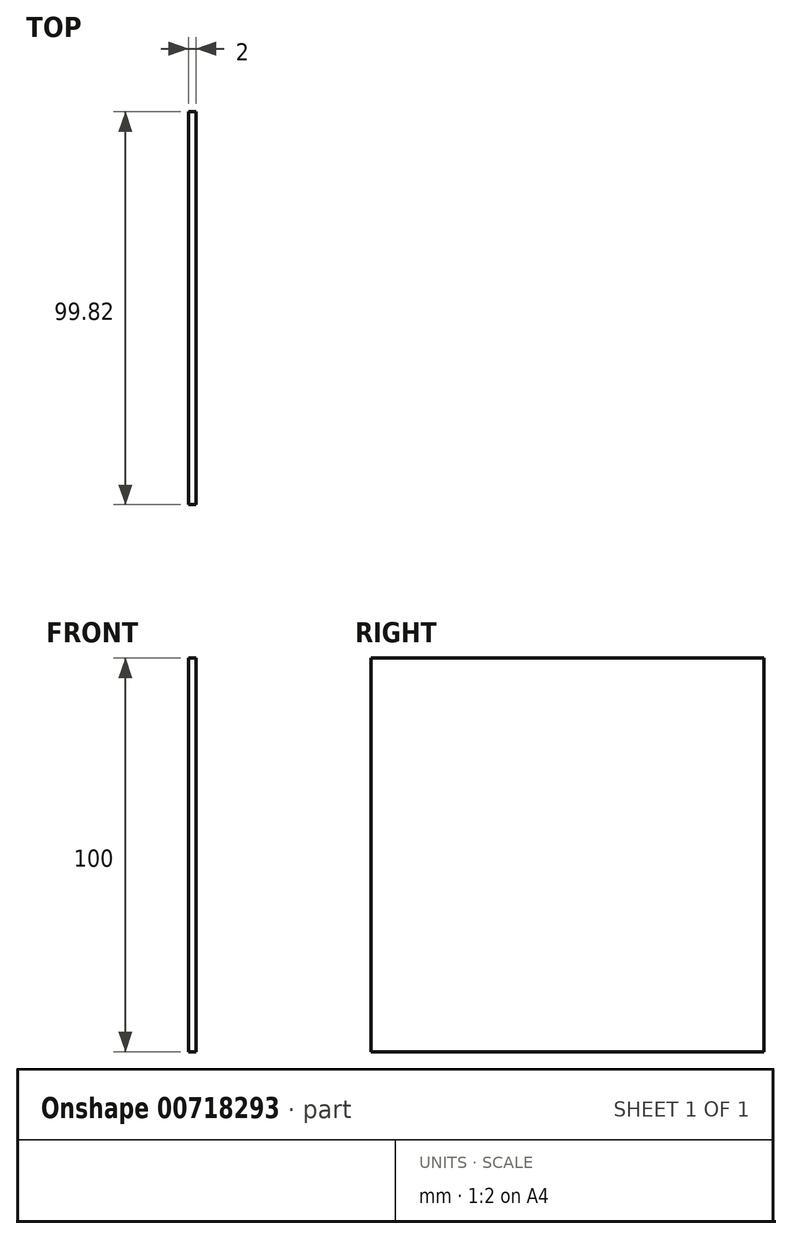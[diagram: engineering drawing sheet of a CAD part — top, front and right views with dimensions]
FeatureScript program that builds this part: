
annotation { "Feature Type Name" : "Feature", "Feature Type Description" : "" }
export const myFeature = defineFeature(function(context is Context, id is Id, definition is map)
    precondition{}
    {
        {
            var Q0;
            Q0=qCreatedBy(makeId("Top.planeOp"),FACE);
            var sketch = newSketch(context, id + "F0", { "sketchPlane" : qUnion([Q0])});
            skCircle(sketch, "E0", {"center": v(0, 0) * mm, "radius": 50 * mm});
            skSolve(sketch);
        }
        {
            var Q0;
            Q0=makeQuery(id+"F0.imprint","IMPRINT",FACE,{"disambiguationData":[TD([[makeQuery(id+"F0.imprint","IMPRINT",EDGE,{"derivedFrom":sQuery(id+"F0.wireOp",EDGE,"E0")}),1.0]])]});
            var sketch = newSketch(context, id + "F1", { "sketchPlane" : qUnion([Q0])});
            skPoint(sketch, "E1", {"position": v(2, 0) * mm});
            skPoint(sketch, "E2.0.1.0", {"position": v(4, 0) * mm});
            skPoint(sketch, "E2.0.2.0", {"position": v(6, 0) * mm});
            skPoint(sketch, "E2.0.3.0", {"position": v(8, 0) * mm});
            skPoint(sketch, "E2.0.4.0", {"position": v(10, 0) * mm});
            skPoint(sketch, "E2.0.5.0", {"position": v(12, 0) * mm});
            skPoint(sketch, "E2.0.6.0", {"position": v(14, 0) * mm});
            skPoint(sketch, "E2.0.7.0", {"position": v(16, 0) * mm});
            skPoint(sketch, "E2.0.8.0", {"position": v(18, 0) * mm});
            skPoint(sketch, "E2.0.9.0", {"position": v(20, 0) * mm});
            skPoint(sketch, "E2.0.10.0", {"position": v(22, 0) * mm});
            skPoint(sketch, "E2.0.11.0", {"position": v(24, 0) * mm});
            skPoint(sketch, "E2.0.12.0", {"position": v(26, 0) * mm});
            skPoint(sketch, "E2.0.13.0", {"position": v(28, 0) * mm});
            skPoint(sketch, "E2.0.14.0", {"position": v(30, 0) * mm});
            skPoint(sketch, "E2.0.15.0", {"position": v(32, 0) * mm});
            skPoint(sketch, "E2.0.16.0", {"position": v(34, 0) * mm});
            skPoint(sketch, "E2.0.17.0", {"position": v(36, 0) * mm});
            skPoint(sketch, "E2.0.18.0", {"position": v(38, 0) * mm});
            skPoint(sketch, "E2.0.19.0", {"position": v(40, 0) * mm});
            skPoint(sketch, "E2.0.20.0", {"position": v(42, 0) * mm});
            skPoint(sketch, "E2.0.21.0", {"position": v(44, 0) * mm});
            skPoint(sketch, "E2.0.22.0", {"position": v(46, 0) * mm});
            skPoint(sketch, "E2.0.23.0", {"position": v(48, 0) * mm});
            skPoint(sketch, "E2.0.24.0", {"position": v(50, 0) * mm});
            skPoint(sketch, "E3", {"position": v(-2, 0) * mm});
            skPoint(sketch, "E4.1.0.0", {"position": v(-4, 0) * mm});
            skPoint(sketch, "E4.2.0.0", {"position": v(-6, 0) * mm});
            skPoint(sketch, "E4.3.0.0", {"position": v(-8, 0) * mm});
            skPoint(sketch, "E4.4.0.0", {"position": v(-10, 0) * mm});
            skPoint(sketch, "E4.5.0.0", {"position": v(-12, 0) * mm});
            skPoint(sketch, "E4.6.0.0", {"position": v(-14, 0) * mm});
            skPoint(sketch, "E4.7.0.0", {"position": v(-16, 0) * mm});
            skPoint(sketch, "E4.8.0.0", {"position": v(-18, 0) * mm});
            skPoint(sketch, "E4.9.0.0", {"position": v(-20, 0) * mm});
            skPoint(sketch, "E4.10.0.0", {"position": v(-22, 0) * mm});
            skPoint(sketch, "E4.11.0.0", {"position": v(-24, 0) * mm});
            skPoint(sketch, "E4.12.0.0", {"position": v(-26, 0) * mm});
            skPoint(sketch, "E4.13.0.0", {"position": v(-28, 0) * mm});
            skPoint(sketch, "E4.14.0.0", {"position": v(-30, 0) * mm});
            skPoint(sketch, "E4.15.0.0", {"position": v(-32, 0) * mm});
            skPoint(sketch, "E4.16.0.0", {"position": v(-34, 0) * mm});
            skPoint(sketch, "E4.17.0.0", {"position": v(-36, 0) * mm});
            skPoint(sketch, "E4.18.0.0", {"position": v(-38, 0) * mm});
            skPoint(sketch, "E4.19.0.0", {"position": v(-40, 0) * mm});
            skPoint(sketch, "E4.20.0.0", {"position": v(-42, 0) * mm});
            skPoint(sketch, "E4.21.0.0", {"position": v(-44, 0) * mm});
            skPoint(sketch, "E4.22.0.0", {"position": v(-46, 0) * mm});
            skPoint(sketch, "E4.23.0.0", {"position": v(-48, 0) * mm});
            skPoint(sketch, "E4.24.0.0", {"position": v(-50, 0) * mm});
            skLineSegment(sketch, "E4.direction1", {"start": v(-2, 0) * mm, "end": v(-4, 0) * mm, "construction": true});
            skLineSegment(sketch, "E5", {"start": v(0, 0) * mm, "end": v(2, 0) * mm});
            skLineSegment(sketch, "E6", {"start": v(8, 0) * mm, "end": v(10, 0) * mm});
            skLineSegment(sketch, "E7", {"start": v(12, 0) * mm, "end": v(14, 0) * mm});
            skLineSegment(sketch, "E8", {"start": v(16, 0) * mm, "end": v(18, 0) * mm});
            skLineSegment(sketch, "E9", {"start": v(14, 0) * mm, "end": v(16, 0) * mm});
            skLineSegment(sketch, "E10", {"start": v(10, 0) * mm, "end": v(12, 0) * mm});
            skLineSegment(sketch, "E11", {"start": v(6, 0) * mm, "end": v(8, 0) * mm});
            skLineSegment(sketch, "E12", {"start": v(2, 0) * mm, "end": v(4, 0) * mm});
            skLineSegment(sketch, "E13", {"start": v(4, 0) * mm, "end": v(6, 0) * mm});
            skLineSegment(sketch, "E14", {"start": v(18, 0) * mm, "end": v(20, 0) * mm});
            skLineSegment(sketch, "E15", {"start": v(20, 0) * mm, "end": v(22, 0) * mm});
            skLineSegment(sketch, "E16", {"start": v(22, 0) * mm, "end": v(24, 0) * mm});
            skLineSegment(sketch, "E17", {"start": v(24, 0) * mm, "end": v(26, 0) * mm});
            skLineSegment(sketch, "E18", {"start": v(26, 0) * mm, "end": v(28, 0) * mm});
            skLineSegment(sketch, "E19", {"start": v(28, 0) * mm, "end": v(30, 0) * mm});
            skLineSegment(sketch, "E20", {"start": v(30, 0) * mm, "end": v(32, 0) * mm});
            skLineSegment(sketch, "E21", {"start": v(32, 0) * mm, "end": v(34, 0) * mm});
            skLineSegment(sketch, "E22", {"start": v(34, 0) * mm, "end": v(36, 0) * mm});
            skLineSegment(sketch, "E23", {"start": v(36, 0) * mm, "end": v(38, 0) * mm});
            skLineSegment(sketch, "E24", {"start": v(38, 0) * mm, "end": v(40, 0) * mm});
            skLineSegment(sketch, "E25", {"start": v(40, 0) * mm, "end": v(42, 0) * mm});
            skLineSegment(sketch, "E26", {"start": v(42, 0) * mm, "end": v(44, 0) * mm});
            skLineSegment(sketch, "E27", {"start": v(44, 0) * mm, "end": v(46, 0) * mm});
            skLineSegment(sketch, "E28", {"start": v(46, 0) * mm, "end": v(48, 0) * mm});
            skLineSegment(sketch, "E29", {"start": v(0, 0) * mm, "end": v(-2, 0) * mm});
            skLineSegment(sketch, "E30.1.0.0", {"start": v(-2, 0) * mm, "end": v(-4, 0) * mm});
            skLineSegment(sketch, "E30.2.0.0", {"start": v(-4, 0) * mm, "end": v(-6, 0) * mm});
            skLineSegment(sketch, "E30.3.0.0", {"start": v(-6, 0) * mm, "end": v(-8, 0) * mm});
            skLineSegment(sketch, "E30.4.0.0", {"start": v(-8, 0) * mm, "end": v(-10, 0) * mm});
            skLineSegment(sketch, "E30.5.0.0", {"start": v(-10, 0) * mm, "end": v(-12, 0) * mm});
            skLineSegment(sketch, "E30.6.0.0", {"start": v(-12, 0) * mm, "end": v(-14, 0) * mm});
            skLineSegment(sketch, "E30.7.0.0", {"start": v(-14, 0) * mm, "end": v(-16, 0) * mm});
            skLineSegment(sketch, "E30.8.0.0", {"start": v(-16, 0) * mm, "end": v(-18, 0) * mm});
            skLineSegment(sketch, "E30.9.0.0", {"start": v(-18, 0) * mm, "end": v(-20, 0) * mm});
            skLineSegment(sketch, "E30.10.0.0", {"start": v(-20, 0) * mm, "end": v(-22, 0) * mm});
            skLineSegment(sketch, "E30.11.0.0", {"start": v(-22, 0) * mm, "end": v(-24, 0) * mm});
            skLineSegment(sketch, "E30.12.0.0", {"start": v(-24, 0) * mm, "end": v(-26, 0) * mm});
            skLineSegment(sketch, "E30.13.0.0", {"start": v(-26, 0) * mm, "end": v(-28, 0) * mm});
            skLineSegment(sketch, "E30.14.0.0", {"start": v(-28, 0) * mm, "end": v(-30, 0) * mm});
            skLineSegment(sketch, "E30.15.0.0", {"start": v(-30, 0) * mm, "end": v(-32, 0) * mm});
            skLineSegment(sketch, "E30.16.0.0", {"start": v(-32, 0) * mm, "end": v(-34, 0) * mm});
            skLineSegment(sketch, "E30.17.0.0", {"start": v(-34, 0) * mm, "end": v(-36, 0) * mm});
            skLineSegment(sketch, "E30.18.0.0", {"start": v(-36, 0) * mm, "end": v(-38, 0) * mm});
            skLineSegment(sketch, "E30.19.0.0", {"start": v(-38, 0) * mm, "end": v(-40, 0) * mm});
            skLineSegment(sketch, "E30.20.0.0", {"start": v(-40, 0) * mm, "end": v(-42, 0) * mm});
            skLineSegment(sketch, "E30.21.0.0", {"start": v(-42, 0) * mm, "end": v(-44, 0) * mm});
            skLineSegment(sketch, "E30.22.0.0", {"start": v(-44, 0) * mm, "end": v(-46, 0) * mm});
            skLineSegment(sketch, "E30.23.0.0", {"start": v(-46, 0) * mm, "end": v(-48, 0) * mm});
            skLineSegment(sketch, "E30.24.0.0", {"start": v(-48, 0) * mm, "end": v(-50, 0) * mm});
            skLineSegment(sketch, "E31", {"start": v(0, 0) * mm, "end": v(0, 50) * mm});
            skLineSegment(sketch, "E32", {"start": v(2, 0) * mm, "end": v(2, 49.91) * mm});
            skLineSegment(sketch, "E33", {"start": v(4, 0) * mm, "end": v(4, 49.83) * mm});
            skLineSegment(sketch, "E34", {"start": v(6, 0) * mm, "end": v(6, 49.6) * mm});
            skLineSegment(sketch, "E35", {"start": v(8, 0) * mm, "end": v(8, 49.33) * mm});
            skLineSegment(sketch, "E36", {"start": v(10, 0) * mm, "end": v(10, 48.95) * mm});
            skLineSegment(sketch, "E37", {"start": v(12, 0) * mm, "end": v(12, 48.5) * mm});
            skLineSegment(sketch, "E38", {"start": v(14, 0) * mm, "end": v(14, 47.96) * mm});
            skLineSegment(sketch, "E39", {"start": v(16, 0) * mm, "end": v(16, 47.33) * mm});
            skLineSegment(sketch, "E40", {"start": v(18, 0) * mm, "end": v(18, 46.61) * mm});
            skLineSegment(sketch, "E41", {"start": v(20, 0) * mm, "end": v(20, 45.78) * mm});
            skLineSegment(sketch, "E42", {"start": v(22, 0) * mm, "end": v(22, 44.86) * mm});
            skLineSegment(sketch, "E43", {"start": v(24, 0) * mm, "end": v(24, 43.82) * mm});
            skLineSegment(sketch, "E44", {"start": v(26, 0) * mm, "end": v(26, 42.66) * mm});
            skLineSegment(sketch, "E45", {"start": v(28, 0) * mm, "end": v(28, 41.4) * mm});
            skLineSegment(sketch, "E46", {"start": v(30, 0) * mm, "end": v(30, 39.94) * mm});
            skLineSegment(sketch, "E47", {"start": v(32, 0) * mm, "end": v(32, 38.4) * mm});
            skLineSegment(sketch, "E48", {"start": v(34, 0) * mm, "end": v(34, 36.6) * mm});
            skLineSegment(sketch, "E49", {"start": v(36, 0) * mm, "end": v(36, 34.65) * mm});
            skLineSegment(sketch, "E50", {"start": v(38, 0) * mm, "end": v(38, 32.47) * mm});
            skLineSegment(sketch, "E51", {"start": v(40, 0) * mm, "end": v(40, 29.93) * mm});
            skLineSegment(sketch, "E52", {"start": v(42, 0) * mm, "end": v(42, 27.04) * mm});
            skLineSegment(sketch, "E53", {"start": v(44, 0) * mm, "end": v(44, 23.66) * mm});
            skLineSegment(sketch, "E54", {"start": v(46, 0) * mm, "end": v(46, 19.48) * mm});
            skLineSegment(sketch, "E55", {"start": v(48, 0) * mm, "end": v(48, 13.88) * mm});
            skLineSegment(sketch, "E56", {"start": v(48, 0) * mm, "end": v(49.75, 0) * mm});
            skLineSegment(sketch, "E57", {"start": v(49.75, 0) * mm, "end": v(49.75, 4.8) * mm});
            skLineSegment(sketch, "E58", {"start": v(49.75, 4.8) * mm, "end": v(48, 4.8) * mm});
            skLineSegment(sketch, "E59", {"start": v(48, 13.88) * mm, "end": v(46, 13.88) * mm});
            skLineSegment(sketch, "E60", {"start": v(46, 19.48) * mm, "end": v(44, 19.48) * mm});
            skLineSegment(sketch, "E61", {"start": v(44, 23.66) * mm, "end": v(42, 23.66) * mm});
            skLineSegment(sketch, "E62", {"start": v(42, 27.04) * mm, "end": v(40, 27.04) * mm});
            skLineSegment(sketch, "E63", {"start": v(40, 29.93) * mm, "end": v(38, 29.93) * mm});
            skLineSegment(sketch, "E64", {"start": v(38, 32.47) * mm, "end": v(36, 32.47) * mm});
            skLineSegment(sketch, "E65", {"start": v(36, 34.65) * mm, "end": v(34, 34.65) * mm});
            skLineSegment(sketch, "E66", {"start": v(34, 36.6) * mm, "end": v(32, 36.6) * mm});
            skLineSegment(sketch, "E67", {"start": v(32, 38.4) * mm, "end": v(30, 38.4) * mm});
            skLineSegment(sketch, "E68", {"start": v(30, 39.94) * mm, "end": v(28, 39.94) * mm});
            skLineSegment(sketch, "E69", {"start": v(28, 41.4) * mm, "end": v(26, 41.4) * mm});
            skLineSegment(sketch, "E70", {"start": v(26, 42.66) * mm, "end": v(24, 42.66) * mm});
            skLineSegment(sketch, "E71", {"start": v(24, 43.82) * mm, "end": v(22, 43.82) * mm});
            skLineSegment(sketch, "E72", {"start": v(22, 44.86) * mm, "end": v(20, 44.86) * mm});
            skLineSegment(sketch, "E73", {"start": v(20, 45.78) * mm, "end": v(18, 45.78) * mm});
            skLineSegment(sketch, "E74", {"start": v(18, 46.61) * mm, "end": v(16, 46.61) * mm});
            skLineSegment(sketch, "E75", {"start": v(16, 47.33) * mm, "end": v(14, 47.33) * mm});
            skLineSegment(sketch, "E76", {"start": v(14, 47.96) * mm, "end": v(12, 47.96) * mm});
            skLineSegment(sketch, "E77", {"start": v(12, 48.5) * mm, "end": v(10, 48.5) * mm});
            skLineSegment(sketch, "E78", {"start": v(10, 48.95) * mm, "end": v(8, 48.95) * mm});
            skLineSegment(sketch, "E79", {"start": v(8, 49.33) * mm, "end": v(6, 49.33) * mm});
            skLineSegment(sketch, "E80", {"start": v(6, 49.6) * mm, "end": v(4, 49.6) * mm});
            skLineSegment(sketch, "E81", {"start": v(4, 49.83) * mm, "end": v(2, 49.83) * mm});
            skLineSegment(sketch, "E82", {"start": v(2, 49.91) * mm, "end": v(0, 49.91) * mm});
            skLineSegment(sketch, "E83.MirrorCS", {"start": v(2, -49.91) * mm, "end": v(0, -49.91) * mm});
            skLineSegment(sketch, "E84.MirrorCS", {"start": v(0, 0) * mm, "end": v(0, -50) * mm});
            skLineSegment(sketch, "E85.MirrorCS", {"start": v(2, 0) * mm, "end": v(2, -49.91) * mm});
            skLineSegment(sketch, "E86.MirrorCS", {"start": v(4, 0) * mm, "end": v(4, -49.83) * mm});
            skLineSegment(sketch, "E87.MirrorCS", {"start": v(6, 0) * mm, "end": v(6, -49.6) * mm});
            skLineSegment(sketch, "E88.MirrorCS", {"start": v(8, 0) * mm, "end": v(8, -49.33) * mm});
            skLineSegment(sketch, "E89.MirrorCS", {"start": v(10, 0) * mm, "end": v(10, -48.95) * mm});
            skLineSegment(sketch, "E90.MirrorCS", {"start": v(12, 0) * mm, "end": v(12, -48.5) * mm});
            skLineSegment(sketch, "E91.MirrorCS", {"start": v(14, 0) * mm, "end": v(14, -47.96) * mm});
            skLineSegment(sketch, "E92.MirrorCS", {"start": v(16, 0) * mm, "end": v(16, -47.33) * mm});
            skLineSegment(sketch, "E93.MirrorCS", {"start": v(18, 0) * mm, "end": v(18, -46.61) * mm});
            skLineSegment(sketch, "E94.MirrorCS", {"start": v(20, 0) * mm, "end": v(20, -45.78) * mm});
            skLineSegment(sketch, "E95.MirrorCS", {"start": v(22, 0) * mm, "end": v(22, -44.86) * mm});
            skLineSegment(sketch, "E96.MirrorCS", {"start": v(24, 0) * mm, "end": v(24, -43.82) * mm});
            skLineSegment(sketch, "E97.MirrorCS", {"start": v(26, 0) * mm, "end": v(26, -42.66) * mm});
            skLineSegment(sketch, "E98.MirrorCS", {"start": v(28, 0) * mm, "end": v(28, -41.4) * mm});
            skLineSegment(sketch, "E99.MirrorCS", {"start": v(30, 0) * mm, "end": v(30, -39.94) * mm});
            skLineSegment(sketch, "E100.MirrorCS", {"start": v(32, 0) * mm, "end": v(32, -38.4) * mm});
            skLineSegment(sketch, "E101.MirrorCS", {"start": v(34, 0) * mm, "end": v(34, -36.6) * mm});
            skLineSegment(sketch, "E102.MirrorCS", {"start": v(36, 0) * mm, "end": v(36, -34.65) * mm});
            skLineSegment(sketch, "E103.MirrorCS", {"start": v(38, 0) * mm, "end": v(38, -32.47) * mm});
            skLineSegment(sketch, "E104.MirrorCS", {"start": v(40, 0) * mm, "end": v(40, -29.93) * mm});
            skLineSegment(sketch, "E105.MirrorCS", {"start": v(42, 0) * mm, "end": v(42, -27.04) * mm});
            skLineSegment(sketch, "E106.MirrorCS", {"start": v(44, 0) * mm, "end": v(44, -23.66) * mm});
            skLineSegment(sketch, "E107.MirrorCS", {"start": v(46, 0) * mm, "end": v(46, -19.48) * mm});
            skLineSegment(sketch, "E108.MirrorCS", {"start": v(48, 0) * mm, "end": v(48, -13.88) * mm});
            skLineSegment(sketch, "E109.MirrorCS", {"start": v(49.75, 0) * mm, "end": v(49.75, -4.8) * mm});
            skLineSegment(sketch, "E110.MirrorCS", {"start": v(49.75, -4.8) * mm, "end": v(48, -4.8) * mm});
            skLineSegment(sketch, "E111.MirrorCS", {"start": v(48, -13.88) * mm, "end": v(46, -13.88) * mm});
            skLineSegment(sketch, "E112.MirrorCS", {"start": v(46, -19.48) * mm, "end": v(44, -19.48) * mm});
            skLineSegment(sketch, "E113.MirrorCS", {"start": v(44, -23.66) * mm, "end": v(42, -23.66) * mm});
            skLineSegment(sketch, "E114.MirrorCS", {"start": v(42, -27.04) * mm, "end": v(40, -27.04) * mm});
            skLineSegment(sketch, "E115.MirrorCS", {"start": v(40, -29.93) * mm, "end": v(38, -29.93) * mm});
            skLineSegment(sketch, "E116.MirrorCS", {"start": v(38, -32.47) * mm, "end": v(36, -32.47) * mm});
            skLineSegment(sketch, "E117.MirrorCS", {"start": v(36, -34.65) * mm, "end": v(34, -34.65) * mm});
            skLineSegment(sketch, "E118.MirrorCS", {"start": v(34, -36.6) * mm, "end": v(32, -36.6) * mm});
            skLineSegment(sketch, "E119.MirrorCS", {"start": v(32, -38.4) * mm, "end": v(30, -38.4) * mm});
            skLineSegment(sketch, "E120.MirrorCS", {"start": v(30, -39.94) * mm, "end": v(28, -39.94) * mm});
            skLineSegment(sketch, "E121.MirrorCS", {"start": v(28, -41.4) * mm, "end": v(26, -41.4) * mm});
            skLineSegment(sketch, "E122.MirrorCS", {"start": v(26, -42.66) * mm, "end": v(24, -42.66) * mm});
            skLineSegment(sketch, "E123.MirrorCS", {"start": v(24, -43.82) * mm, "end": v(22, -43.82) * mm});
            skLineSegment(sketch, "E124.MirrorCS", {"start": v(22, -44.86) * mm, "end": v(20, -44.86) * mm});
            skLineSegment(sketch, "E125.MirrorCS", {"start": v(20, -45.78) * mm, "end": v(18, -45.78) * mm});
            skLineSegment(sketch, "E126.MirrorCS", {"start": v(18, -46.61) * mm, "end": v(16, -46.61) * mm});
            skLineSegment(sketch, "E127.MirrorCS", {"start": v(16, -47.33) * mm, "end": v(14, -47.33) * mm});
            skLineSegment(sketch, "E128.MirrorCS", {"start": v(14, -47.96) * mm, "end": v(12, -47.96) * mm});
            skLineSegment(sketch, "E129.MirrorCS", {"start": v(12, -48.5) * mm, "end": v(10, -48.5) * mm});
            skLineSegment(sketch, "E130.MirrorCS", {"start": v(10, -48.95) * mm, "end": v(8, -48.95) * mm});
            skLineSegment(sketch, "E131.MirrorCS", {"start": v(8, -49.33) * mm, "end": v(6, -49.33) * mm});
            skLineSegment(sketch, "E132.MirrorCS", {"start": v(6, -49.6) * mm, "end": v(4, -49.6) * mm});
            skLineSegment(sketch, "E133.MirrorCS", {"start": v(4, -49.83) * mm, "end": v(2, -49.83) * mm});
            skLineSegment(sketch, "E134.MirrorCS", {"start": v(-2, 0) * mm, "end": v(-2, 49.91) * mm});
            skLineSegment(sketch, "E135.MirrorCS", {"start": v(-4, 0) * mm, "end": v(-4, 49.83) * mm});
            skLineSegment(sketch, "E136.MirrorCS", {"start": v(-6, 0) * mm, "end": v(-6, 49.6) * mm});
            skLineSegment(sketch, "E137.MirrorCS", {"start": v(-8, 0) * mm, "end": v(-8, 49.33) * mm});
            skLineSegment(sketch, "E138.MirrorCS", {"start": v(-10, 0) * mm, "end": v(-10, 48.95) * mm});
            skLineSegment(sketch, "E139.MirrorCS", {"start": v(-12, 0) * mm, "end": v(-12, 48.5) * mm});
            skLineSegment(sketch, "E140.MirrorCS", {"start": v(-14, 0) * mm, "end": v(-14, 47.96) * mm});
            skLineSegment(sketch, "E141.MirrorCS", {"start": v(-16, 0) * mm, "end": v(-16, 47.33) * mm});
            skLineSegment(sketch, "E142.MirrorCS", {"start": v(-18, 0) * mm, "end": v(-18, 46.61) * mm});
            skLineSegment(sketch, "E143.MirrorCS", {"start": v(-20, 0) * mm, "end": v(-20, 45.78) * mm});
            skLineSegment(sketch, "E144.MirrorCS", {"start": v(-22, 0) * mm, "end": v(-22, 44.86) * mm});
            skLineSegment(sketch, "E145.MirrorCS", {"start": v(-24, 0) * mm, "end": v(-24, 43.82) * mm});
            skLineSegment(sketch, "E146.MirrorCS", {"start": v(-26, 0) * mm, "end": v(-26, 42.66) * mm});
            skLineSegment(sketch, "E147.MirrorCS", {"start": v(-28, 0) * mm, "end": v(-28, 41.4) * mm});
            skLineSegment(sketch, "E148.MirrorCS", {"start": v(-30, 0) * mm, "end": v(-30, 39.94) * mm});
            skLineSegment(sketch, "E149.MirrorCS", {"start": v(-32, 0) * mm, "end": v(-32, 38.4) * mm});
            skLineSegment(sketch, "E150.MirrorCS", {"start": v(-34, 0) * mm, "end": v(-34, 36.6) * mm});
            skLineSegment(sketch, "E151.MirrorCS", {"start": v(-36, 0) * mm, "end": v(-36, 34.65) * mm});
            skLineSegment(sketch, "E152.MirrorCS", {"start": v(-38, 0) * mm, "end": v(-38, 32.47) * mm});
            skLineSegment(sketch, "E153.MirrorCS", {"start": v(-42, 0) * mm, "end": v(-42, 27.04) * mm});
            skLineSegment(sketch, "E154.MirrorCS", {"start": v(-44, 0) * mm, "end": v(-44, 23.66) * mm});
            skLineSegment(sketch, "E155.MirrorCS", {"start": v(-46, 0) * mm, "end": v(-46, 19.48) * mm});
            skLineSegment(sketch, "E156.MirrorCS", {"start": v(-48, 0) * mm, "end": v(-48, 13.88) * mm});
            skLineSegment(sketch, "E157.MirrorCS", {"start": v(-49.75, 0) * mm, "end": v(-49.75, 4.8) * mm});
            skLineSegment(sketch, "E158.MirrorCS", {"start": v(-40, 0) * mm, "end": v(-40, 29.93) * mm});
            skLineSegment(sketch, "E159.MirrorCS", {"start": v(-49.75, 0) * mm, "end": v(-49.75, -4.8) * mm});
            skLineSegment(sketch, "E160.MirrorCS", {"start": v(-48, 0) * mm, "end": v(-48, -13.88) * mm});
            skLineSegment(sketch, "E161.MirrorCS", {"start": v(-46, 0) * mm, "end": v(-46, -19.48) * mm});
            skLineSegment(sketch, "E162.MirrorCS", {"start": v(-44, 0) * mm, "end": v(-44, -23.66) * mm});
            skLineSegment(sketch, "E163.MirrorCS", {"start": v(-42, 0) * mm, "end": v(-42, -27.04) * mm});
            skLineSegment(sketch, "E164.MirrorCS", {"start": v(-40, 0) * mm, "end": v(-40, -29.93) * mm});
            skLineSegment(sketch, "E165.MirrorCS", {"start": v(-38, 0) * mm, "end": v(-38, -32.47) * mm});
            skLineSegment(sketch, "E166.MirrorCS", {"start": v(-36, 0) * mm, "end": v(-36, -34.65) * mm});
            skLineSegment(sketch, "E167.MirrorCS", {"start": v(-34, 0) * mm, "end": v(-34, -36.6) * mm});
            skLineSegment(sketch, "E168.MirrorCS", {"start": v(-32, 0) * mm, "end": v(-32, -38.4) * mm});
            skLineSegment(sketch, "E169.MirrorCS", {"start": v(-30, 0) * mm, "end": v(-30, -39.94) * mm});
            skLineSegment(sketch, "E170.MirrorCS", {"start": v(-28, 0) * mm, "end": v(-28, -41.4) * mm});
            skLineSegment(sketch, "E171.MirrorCS", {"start": v(-26, 0) * mm, "end": v(-26, -42.66) * mm});
            skLineSegment(sketch, "E172.MirrorCS", {"start": v(-24, 0) * mm, "end": v(-24, -43.82) * mm});
            skLineSegment(sketch, "E173.MirrorCS", {"start": v(-22, 0) * mm, "end": v(-22, -44.86) * mm});
            skLineSegment(sketch, "E174.MirrorCS", {"start": v(-20, 0) * mm, "end": v(-20, -45.78) * mm});
            skLineSegment(sketch, "E175.MirrorCS", {"start": v(-18, 0) * mm, "end": v(-18, -46.61) * mm});
            skLineSegment(sketch, "E176.MirrorCS", {"start": v(-16, 0) * mm, "end": v(-16, -47.33) * mm});
            skLineSegment(sketch, "E177.MirrorCS", {"start": v(-14, 0) * mm, "end": v(-14, -47.96) * mm});
            skLineSegment(sketch, "E178.MirrorCS", {"start": v(-12, 0) * mm, "end": v(-12, -48.5) * mm});
            skLineSegment(sketch, "E179.MirrorCS", {"start": v(-10, 0) * mm, "end": v(-10, -48.95) * mm});
            skLineSegment(sketch, "E180.MirrorCS", {"start": v(-8, 0) * mm, "end": v(-8, -49.33) * mm});
            skLineSegment(sketch, "E181.MirrorCS", {"start": v(-6, 0) * mm, "end": v(-6, -49.6) * mm});
            skLineSegment(sketch, "E182.MirrorCS", {"start": v(-4, 0) * mm, "end": v(-4, -49.83) * mm});
            skLineSegment(sketch, "E183.MirrorCS", {"start": v(-2, 0) * mm, "end": v(-2, -49.91) * mm});
            skLineSegment(sketch, "E184.MirrorCS", {"start": v(-49.75, -4.8) * mm, "end": v(-48, -4.8) * mm});
            skLineSegment(sketch, "E185.MirrorCS", {"start": v(-48, -13.88) * mm, "end": v(-46, -13.88) * mm});
            skLineSegment(sketch, "E186.MirrorCS", {"start": v(-46, -19.48) * mm, "end": v(-44, -19.48) * mm});
            skLineSegment(sketch, "E187.MirrorCS", {"start": v(-44, -23.66) * mm, "end": v(-42, -23.66) * mm});
            skLineSegment(sketch, "E188.MirrorCS", {"start": v(-42, -27.04) * mm, "end": v(-40, -27.04) * mm});
            skLineSegment(sketch, "E189.MirrorCS", {"start": v(-40, -29.93) * mm, "end": v(-38, -29.93) * mm});
            skLineSegment(sketch, "E190.MirrorCS", {"start": v(-38, -32.47) * mm, "end": v(-36, -32.47) * mm});
            skLineSegment(sketch, "E191.MirrorCS", {"start": v(-36, -34.65) * mm, "end": v(-34, -34.65) * mm});
            skLineSegment(sketch, "E192.MirrorCS", {"start": v(-34, -36.6) * mm, "end": v(-32, -36.6) * mm});
            skLineSegment(sketch, "E193.MirrorCS", {"start": v(-32, -38.4) * mm, "end": v(-30, -38.4) * mm});
            skLineSegment(sketch, "E194.MirrorCS", {"start": v(-30, -39.94) * mm, "end": v(-28, -39.94) * mm});
            skLineSegment(sketch, "E195.MirrorCS", {"start": v(-28, -41.4) * mm, "end": v(-26, -41.4) * mm});
            skLineSegment(sketch, "E196.MirrorCS", {"start": v(-26, -42.66) * mm, "end": v(-24, -42.66) * mm});
            skLineSegment(sketch, "E197.MirrorCS", {"start": v(-24, -43.82) * mm, "end": v(-22, -43.82) * mm});
            skLineSegment(sketch, "E198.MirrorCS", {"start": v(-22, -44.86) * mm, "end": v(-20, -44.86) * mm});
            skLineSegment(sketch, "E199.MirrorCS", {"start": v(-20, -45.78) * mm, "end": v(-18, -45.78) * mm});
            skLineSegment(sketch, "E200.MirrorCS", {"start": v(-18, -46.61) * mm, "end": v(-16, -46.61) * mm});
            skLineSegment(sketch, "E201.MirrorCS", {"start": v(-12, -48.5) * mm, "end": v(-10, -48.5) * mm});
            skLineSegment(sketch, "E202.MirrorCS", {"start": v(-10, -48.95) * mm, "end": v(-8, -48.95) * mm});
            skLineSegment(sketch, "E203.MirrorCS", {"start": v(-8, -49.33) * mm, "end": v(-6, -49.33) * mm});
            skLineSegment(sketch, "E204.MirrorCS", {"start": v(-6, -49.6) * mm, "end": v(-4, -49.6) * mm});
            skLineSegment(sketch, "E205.MirrorCS", {"start": v(-4, -49.83) * mm, "end": v(-2, -49.83) * mm});
            skLineSegment(sketch, "E206.MirrorCS", {"start": v(-2, -49.91) * mm, "end": v(0, -49.91) * mm});
            skLineSegment(sketch, "E207.MirrorCS", {"start": v(-14, -47.96) * mm, "end": v(-12, -47.96) * mm});
            skLineSegment(sketch, "E208.MirrorCS", {"start": v(-16, -47.33) * mm, "end": v(-14, -47.33) * mm});
            skLineSegment(sketch, "E209.MirrorCS", {"start": v(-49.75, 4.8) * mm, "end": v(-48, 4.8) * mm});
            skLineSegment(sketch, "E210.MirrorCS", {"start": v(-48, 13.88) * mm, "end": v(-46, 13.88) * mm});
            skLineSegment(sketch, "E211.MirrorCS", {"start": v(-46, 19.48) * mm, "end": v(-44, 19.48) * mm});
            skLineSegment(sketch, "E212.MirrorCS", {"start": v(-44, 23.66) * mm, "end": v(-42, 23.66) * mm});
            skLineSegment(sketch, "E213.MirrorCS", {"start": v(-42, 27.04) * mm, "end": v(-40, 27.04) * mm});
            skLineSegment(sketch, "E214.MirrorCS", {"start": v(-40, 29.93) * mm, "end": v(-38, 29.93) * mm});
            skLineSegment(sketch, "E215.MirrorCS", {"start": v(-38, 32.47) * mm, "end": v(-36, 32.47) * mm});
            skLineSegment(sketch, "E216.MirrorCS", {"start": v(-36, 34.65) * mm, "end": v(-34, 34.65) * mm});
            skLineSegment(sketch, "E217.MirrorCS", {"start": v(-34, 36.6) * mm, "end": v(-32, 36.6) * mm});
            skLineSegment(sketch, "E218.MirrorCS", {"start": v(-32, 38.4) * mm, "end": v(-30, 38.4) * mm});
            skLineSegment(sketch, "E219.MirrorCS", {"start": v(-26, 42.66) * mm, "end": v(-24, 42.66) * mm});
            skLineSegment(sketch, "E220.MirrorCS", {"start": v(-24, 43.82) * mm, "end": v(-22, 43.82) * mm});
            skLineSegment(sketch, "E221.MirrorCS", {"start": v(-22, 44.86) * mm, "end": v(-20, 44.86) * mm});
            skLineSegment(sketch, "E222.MirrorCS", {"start": v(-20, 45.78) * mm, "end": v(-18, 45.78) * mm});
            skLineSegment(sketch, "E223.MirrorCS", {"start": v(-18, 46.61) * mm, "end": v(-16, 46.61) * mm});
            skLineSegment(sketch, "E224.MirrorCS", {"start": v(-16, 47.33) * mm, "end": v(-14, 47.33) * mm});
            skLineSegment(sketch, "E225.MirrorCS", {"start": v(-14, 47.96) * mm, "end": v(-12, 47.96) * mm});
            skLineSegment(sketch, "E226.MirrorCS", {"start": v(-12, 48.5) * mm, "end": v(-10, 48.5) * mm});
            skLineSegment(sketch, "E227.MirrorCS", {"start": v(-10, 48.95) * mm, "end": v(-8, 48.95) * mm});
            skLineSegment(sketch, "E228.MirrorCS", {"start": v(-8, 49.33) * mm, "end": v(-6, 49.33) * mm});
            skLineSegment(sketch, "E229.MirrorCS", {"start": v(-6, 49.6) * mm, "end": v(-4, 49.6) * mm});
            skLineSegment(sketch, "E230.MirrorCS", {"start": v(-2, 49.91) * mm, "end": v(0, 49.91) * mm});
            skLineSegment(sketch, "E231.MirrorCS", {"start": v(-4, 49.83) * mm, "end": v(-2, 49.83) * mm});
            skLineSegment(sketch, "E232.MirrorCS", {"start": v(-28, 41.4) * mm, "end": v(-26, 41.4) * mm});
            skLineSegment(sketch, "E233.MirrorCS", {"start": v(-30, 39.94) * mm, "end": v(-28, 39.94) * mm});
            skLineSegment(sketch, "E234", {"start": v(0, 50) * mm, "end": v(0, 0) * mm});
            skSolve(sketch);
        }
        {
            var Q0;
            {var subQ3=sQuery(id+"F1.wireOp",EDGE,"E5");Q0=makeQuery(id+"F1.imprint","IMPRINT",FACE,{"disambiguationData":[TD([[makeQuery(id+"F1.imprint","IMPRINT",EDGE,{"derivedFrom":subQ3}),1.0]])]});}
            var Q1;
            {var subQ3=sQuery(id+"F1.wireOp",EDGE,"E5");Q1=makeQuery(id+"F1.imprint","IMPRINT",FACE,{"disambiguationData":[TD([[makeQuery(id+"F1.imprint","IMPRINT",EDGE,{"derivedFrom":subQ3}),-1.0]])]});}
            extrude(context, id + "F2", {"entities" : qUnion([Q0, Q1]), "depth" : 100 * mm, "offsetDistance" : 25 * mm});
        }
    });
